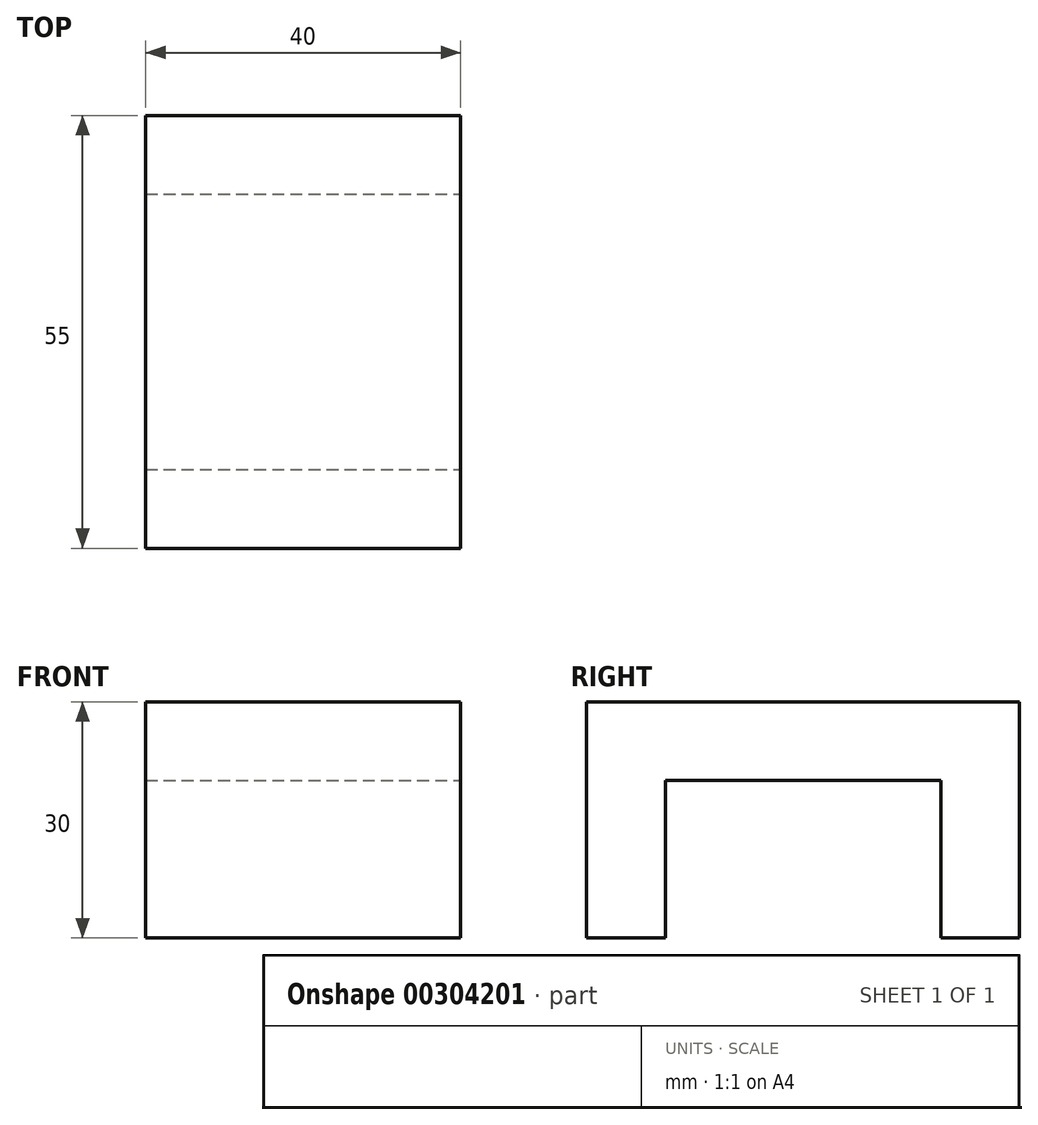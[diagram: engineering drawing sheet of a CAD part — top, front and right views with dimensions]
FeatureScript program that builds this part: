
annotation { "Feature Type Name" : "Feature", "Feature Type Description" : "" }
export const myFeature = defineFeature(function(context is Context, id is Id, definition is map)
    precondition{}
    {
        {
            var Q0;
            Q0=qCreatedBy(makeId("Top.planeOp"),FACE);
            var sketch = newSketch(context, id + "F0", { "sketchPlane" : qUnion([Q0])});
            skLineSegment(sketch, "E0.bottom", {"start": v(-20.33, 28.14) * mm, "end": v(19.67, 28.14) * mm});
            skLineSegment(sketch, "E0.top", {"start": v(-20.33, -26.86) * mm, "end": v(19.67, -26.86) * mm});
            skLineSegment(sketch, "E0.left", {"start": v(-20.33, 28.14) * mm, "end": v(-20.33, -26.86) * mm});
            skLineSegment(sketch, "E0.right", {"start": v(19.67, 28.14) * mm, "end": v(19.67, -26.86) * mm});
            skLineSegment(sketch, "E1.bottom", {"start": v(-20.33, 18.14) * mm, "end": v(19.67, 18.14) * mm});
            skLineSegment(sketch, "E1.top", {"start": v(-20.33, -16.86) * mm, "end": v(19.67, -16.86) * mm});
            skLineSegment(sketch, "E1.left", {"start": v(-20.33, 18.14) * mm, "end": v(-20.33, -16.86) * mm});
            skLineSegment(sketch, "E1.right", {"start": v(19.67, 18.14) * mm, "end": v(19.67, -16.86) * mm});
            skSolve(sketch);
        }
        {
            var Q0;
            Q0=makeQuery(id+"F0.imprint","IMPRINT",FACE,{"disambiguationData":[TD([[makeQuery(id+"F0.imprint","IMPRINT",EDGE,{"derivedFrom":sQuery(id+"F0.wireOp",EDGE,"E1.bottom")}),-1.0]])]});
            extrude(context, id + "F1", {"entities" : qUnion([Q0]), "depth" : 30 * mm});
        }
        {
            var Q0;
            Q0 = qSketchRegion(id + "F0", true);
            extrude(context, id + "F2", {"entities" : qUnion([Q0]), "operationType" : NewBodyOperationType.ADD, "depth" : 30 * mm});
        }
        {
            var Q0;
            {var subQ0=sQuery(id+"F0.wireOp",EDGE,"E1.right");var subQ1=sQuery(id+"F0.wireOp",EDGE,"E1.left");Q0=makeQuery(id+"F2.boolean.opBoolean","MERGE",FACE,{"derivedFrom":[makeQuery(id+"F1.opExtrude","CAP_FACE",FACE,{"disambiguationData":[OSD([sQuery(id+"F0.wireOp",EDGE,"E1.bottom"),sQuery(id+"F0.wireOp",EDGE,"E1.top"),subQ1,subQ0])],"isStart":true}),makeQuery(id+"F2.opExtrude","CAP_FACE",FACE,{"disambiguationData":[OSD([sQuery(id+"F0.wireOp",EDGE,"E0.bottom"),sQuery(id+"F0.wireOp",EDGE,"E0.top"),sQuery(id+"F0.wireOp",EDGE,"E0.left"),sQuery(id+"F0.wireOp",EDGE,"E0.right"),subQ1,subQ0])],"isStart":true})]});}
            var sketch = newSketch(context, id + "F3", { "sketchPlane" : qUnion([Q0])});
            skLineSegment(sketch, "E2.bottom", {"start": v(-20.33, 16.86) * mm, "end": v(19.67, 16.86) * mm});
            skLineSegment(sketch, "E2.top", {"start": v(-20.33, -18.14) * mm, "end": v(19.67, -18.14) * mm});
            skLineSegment(sketch, "E2.left", {"start": v(-20.33, 16.86) * mm, "end": v(-20.33, -18.14) * mm});
            skLineSegment(sketch, "E2.right", {"start": v(19.67, 16.86) * mm, "end": v(19.67, -18.14) * mm});
            skSolve(sketch);
        }
        {
            var Q0;
            Q0 = qSketchRegion(id + "F3", true);
            extrude(context, id + "F4", {"entities" : qUnion([Q0]), "operationType" : NewBodyOperationType.REMOVE, "oppositeDirection" : true, "depth" : 20 * mm});
        }
    });
